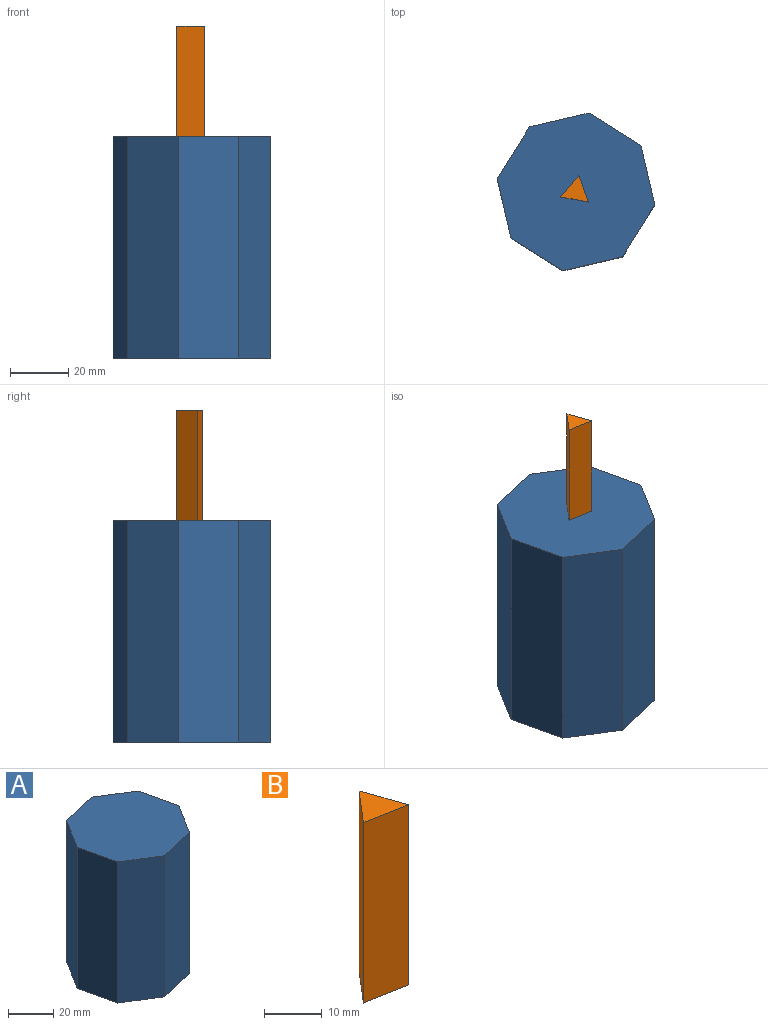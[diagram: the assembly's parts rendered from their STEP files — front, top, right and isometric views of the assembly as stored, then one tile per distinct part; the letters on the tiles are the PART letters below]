
ASSEMBLY  parts=2 mates=1
PART A: 10 faces, bbox 54.2x54.2x76.2 mm
  f0: plane 76.2x20.49mm, normal (0.97,0.23,0), area 1603.4mm2, adj f1,f7,f8,f9
  f1: plane 76.2x17.87mm, normal (0.53,0.85,0), area 1603.4mm2, adj f0,f2,f8,f9
  f2: plane 76.2x20.49mm, normal (-0.23,0.97,0), area 1603.4mm2, adj f1,f3,f8,f9
  f3: plane 76.2x17.87mm, normal (-0.85,0.53,0), area 1603.4mm2, adj f2,f4,f8,f9
  f4: plane 76.2x20.49mm, normal (-0.97,-0.23,0), area 1603.4mm2, adj f3,f5,f8,f9
  f5: plane 76.2x17.87mm, normal (-0.53,-0.85,0), area 1603.4mm2, adj f4,f6,f8,f9
  f6: plane 76.2x20.49mm, normal (0.23,-0.97,0), area 1603.4mm2, adj f5,f7,f8,f9
  f7: plane 76.2x17.87mm, normal (0.85,-0.53,0), area 1603.4mm2, adj f0,f6,f8,f9
  f8: plane 54.25x54.25mm, normal (0,0,1), area 2137.9mm2, adj f0,f1,f2,f3,f4,f5,f6,f7
  f9: plane 54.25x54.25mm, normal (0,0,-1), area 2137.9mm2, adj f0,f1,f2,f3,f4,f5,f6,f7
PART B: 5 faces, bbox 9.4x9x38.1 mm
  f0: plane 38.1x9.36mm, normal (-0.18,-0.98,0), area 362.9mm2, adj f1,f2,f3,f4
  f1: plane 38.1x8.98mm, normal (0.94,0.33,0), area 362.9mm2, adj f0,f2,f3,f4
  f2: plane 38.1x7.24mm, normal (-0.76,0.65,0), area 362.9mm2, adj f0,f1,f3,f4
  f3: plane 9.36x8.98mm, normal (0,0,1), area 39.3mm2, adj f0,f1,f2
  f4: plane 9.36x8.98mm, normal (0,0,-1), area 39.3mm2, adj f0,f1,f2
PLACE A t=(8.41,11.21,5.86)mm
PLACE B t=(12.37,23.18,82.06)mm
MATE fastened A.f8 <-> B.f4  axis (0,0,1) through (-32.95,51.41,82.06)mm
